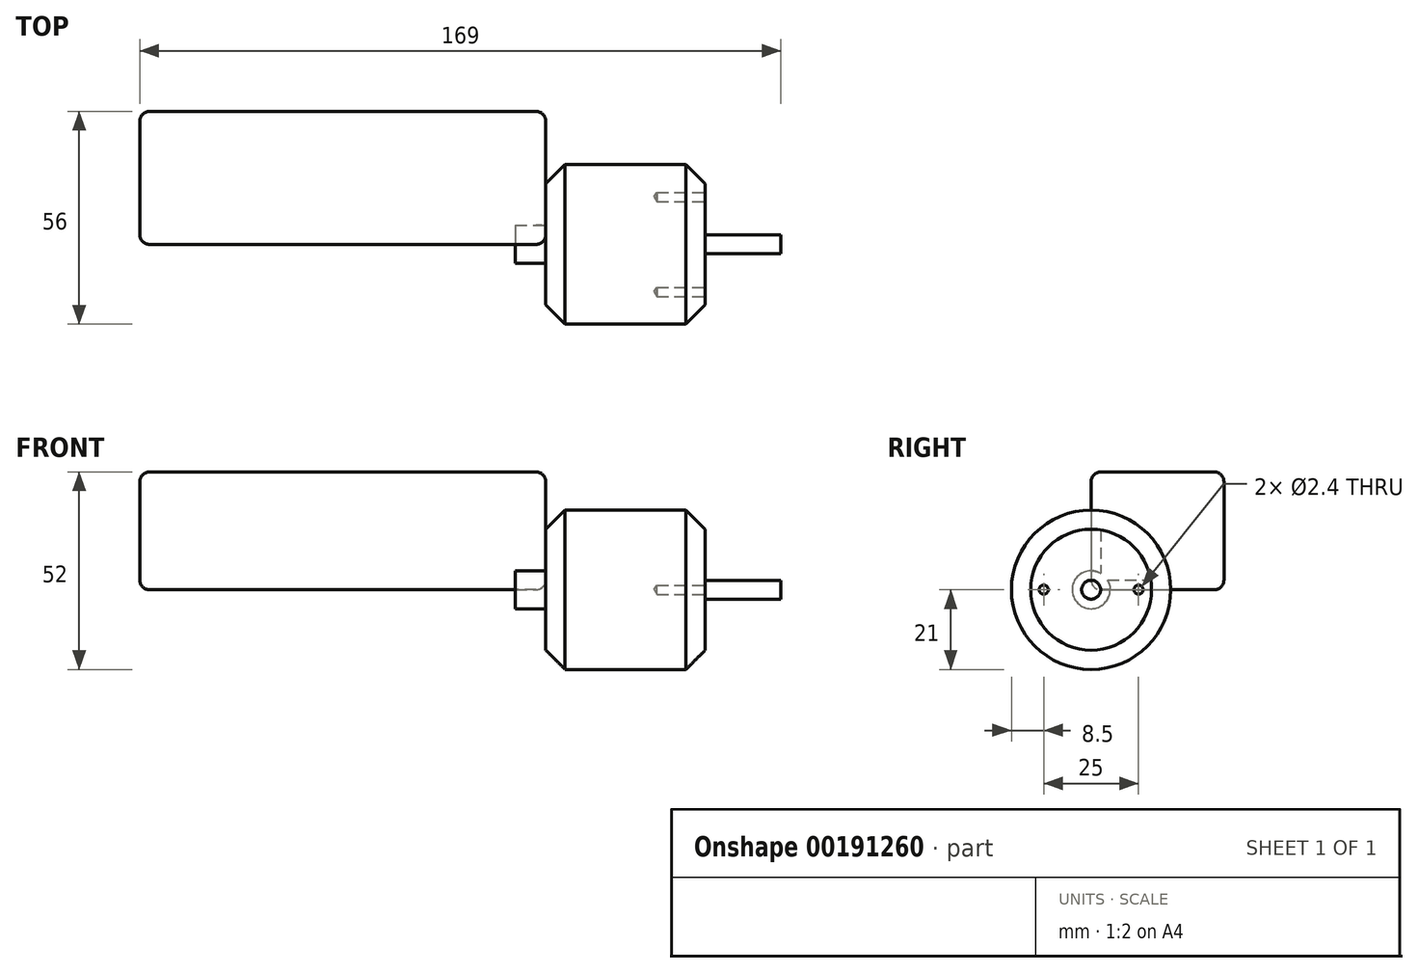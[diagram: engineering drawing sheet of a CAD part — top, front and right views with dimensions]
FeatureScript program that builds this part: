
annotation { "Feature Type Name" : "Feature", "Feature Type Description" : "" }
export const myFeature = defineFeature(function(context is Context, id is Id, definition is map)
    precondition{}
    {
        {
            var Q0;
            Q0=qCreatedBy(makeId("Right.planeOp"),FACE);
            var sketch = newSketch(context, id + "F0", { "sketchPlane" : qUnion([Q0])});
            skCircle(sketch, "E0", {"center": v(0, 0) * mm, "radius": 21 * mm});
            skSolve(sketch);
        }
        {
            var Q0;
            Q0 = qSketchRegion(id + "F0", true);
            extrude(context, id + "F1", {"entities" : qUnion([Q0]), "depth" : 42 * mm});
        }
        {
            var Q0;
            Q0=makeQuery(id+"F1.opExtrude","CAP_EDGE",EDGE,{"disambiguationData":[OSD([sQuery(id+"F0.wireOp",EDGE,"E0")])],"isStart":true});
            var Q1;
            Q1=makeQuery(id+"F1.opExtrude","CAP_EDGE",EDGE,{"disambiguationData":[OSD([sQuery(id+"F0.wireOp",EDGE,"E0")])],"isStart":false});
            chamfer(context, id + "F2", {"entities" : qUnion([Q0, Q1]), "chamferType" : ChamferType.TWO_OFFSETS, "width1" : 5.08 * mm, "oppositeDirection" : false, "width2" : 5.08 * mm});
        }
        {
            var Q0;
            Q0=makeQuery(id+"F1.opExtrude","CAP_FACE",FACE,{"disambiguationData":[OSD([sQuery(id+"F0.wireOp",EDGE,"E0")])],"isStart":false});
            var sketch = newSketch(context, id + "F3", { "sketchPlane" : qUnion([Q0])});
            skCircle(sketch, "E1", {"center": v(0, 0) * mm, "radius": 2.5 * mm});
            skSolve(sketch);
        }
        {
            var Q0;
            Q0 = qSketchRegion(id + "F3", true);
            extrude(context, id + "F4", {"entities" : qUnion([Q0]), "operationType" : NewBodyOperationType.ADD, "depth" : 20 * mm});
        }
        {
            var Q0;
            Q0=makeQuery(id+"F1.opExtrude","CAP_FACE",FACE,{"disambiguationData":[OSD([sQuery(id+"F0.wireOp",EDGE,"E0")])],"isStart":false});
            var sketch = newSketch(context, id + "F5", { "sketchPlane" : qUnion([Q0])});
            skPoint(sketch, "E2", {"position": v(12.5, 0) * mm});
            skPoint(sketch, "E3.1.0", {"position": v(-12.5, 0) * mm});
            skPoint(sketch, "E3.center", {"position": v(0, 0) * mm});
            skSolve(sketch);
        }
        {
            var Q0;
            Q0=sQuery(id+"F5.wireOp",VERTEX,"E3.1.0");
            var Q1;
            Q1=sQuery(id+"F5.wireOp",VERTEX,"E2");
            var Q2;
            Q2=makeQuery(id+"F1.opExtrude","SWEPT_BODY",BODY,{"disambiguationData":[OSD([sQuery(id+"F0.wireOp",EDGE,"E0")])]});
            hole(context, id + "F6", {"style" : HoleStyle.SIMPLE, "endStyle" : HoleEndStyle.BLIND, "standardTappedOrClearance" : lookupTablePath({ "standard" : "ISO", "engagement" : "75%", "pitch" : "0.6 mm", "size" : "M3", "type" : "Tapped" }), "standardBlindInLast" : lookupTablePath({ "standard" : "ISO", "engagement" : "75%", "pitch" : "0.6 mm", "size" : "M3", "type" : "Tapped" }), "holeDiameter" : 2.4 * mm, "holeDepth" : 12.7 * mm, "locations" : qUnion([Q0, Q1]), "scope" : qUnion([Q2])});
        }
        {
            var Q0;
            Q0=qCreatedBy(makeId("Top.planeOp"),FACE);
            var sketch = newSketch(context, id + "F7", { "sketchPlane" : qUnion([Q0])});
            skLineSegment(sketch, "E4.bottom", {"start": v(0, 0) * mm, "end": v(-107, 0) * mm});
            skLineSegment(sketch, "E4.top", {"start": v(0, 35) * mm, "end": v(-107, 35) * mm});
            skLineSegment(sketch, "E4.left", {"start": v(0, 0) * mm, "end": v(0, 35) * mm});
            skLineSegment(sketch, "E4.right", {"start": v(-107, 0) * mm, "end": v(-107, 35) * mm});
            skSolve(sketch);
        }
        {
            var Q0;
            Q0=makeQuery(id+"F7.imprint","IMPRINT",FACE,{"disambiguationData":[TD([[makeQuery(id+"F7.imprint","IMPRINT",EDGE,{"derivedFrom":sQuery(id+"F7.wireOp",EDGE,"E4.bottom")}),-1.0]])]});
            extrude(context, id + "F8", {"entities" : qUnion([Q0]), "depth" : 31 * mm});
        }
        {
            var Q0;
            Q0=makeQuery(id+"F8.opExtrude","CAP_FACE",FACE,{"disambiguationData":[OSD([sQuery(id+"F7.wireOp",EDGE,"E4.bottom"),sQuery(id+"F7.wireOp",EDGE,"E4.top"),sQuery(id+"F7.wireOp",EDGE,"E4.left"),sQuery(id+"F7.wireOp",EDGE,"E4.right")])],"isStart":false});
            var Q1;
            Q1=makeQuery(id+"F8.opExtrude","CAP_FACE",FACE,{"disambiguationData":[OSD([sQuery(id+"F7.wireOp",EDGE,"E4.bottom"),sQuery(id+"F7.wireOp",EDGE,"E4.top"),sQuery(id+"F7.wireOp",EDGE,"E4.left"),sQuery(id+"F7.wireOp",EDGE,"E4.right")])],"isStart":true});
            var Q2;
            Q2=makeQuery(id+"F8.opExtrude","SWEPT_FACE",FACE,{"disambiguationData":[OSD([sQuery(id+"F7.wireOp",EDGE,"E4.top")])]});
            var Q3;
            Q3=makeQuery(id+"F8.opExtrude","SWEPT_FACE",FACE,{"disambiguationData":[OSD([sQuery(id+"F7.wireOp",EDGE,"E4.bottom")])]});
            fillet(context, id + "F9", {"entities" : qUnion([Q0, Q1, Q2, Q3]), "radius" : 2.54 * mm, "tangentPropagation" : true, "allowEdgeOverflow" : false});
        }
        {
            var Q0;
            Q0=makeQuery(id+"F1.opExtrude","CAP_FACE",FACE,{"disambiguationData":[OSD([sQuery(id+"F0.wireOp",EDGE,"E0")])],"isStart":true});
            var sketch = newSketch(context, id + "F10", { "sketchPlane" : qUnion([Q0])});
            skCircle(sketch, "E5", {"center": v(0, 0) * mm, "radius": 5 * mm});
            skSolve(sketch);
        }
        {
            var Q0;
            Q0=makeQuery(id+"F10.imprint","IMPRINT",FACE,{"disambiguationData":[TD([[makeQuery(id+"F10.imprint","IMPRINT",EDGE,{"derivedFrom":sQuery(id+"F10.wireOp",EDGE,"E5")}),1.0]])]});
            extrude(context, id + "F11", {"entities" : qUnion([Q0]), "operationType" : NewBodyOperationType.ADD, "depth" : 8 * mm});
        }
    });
